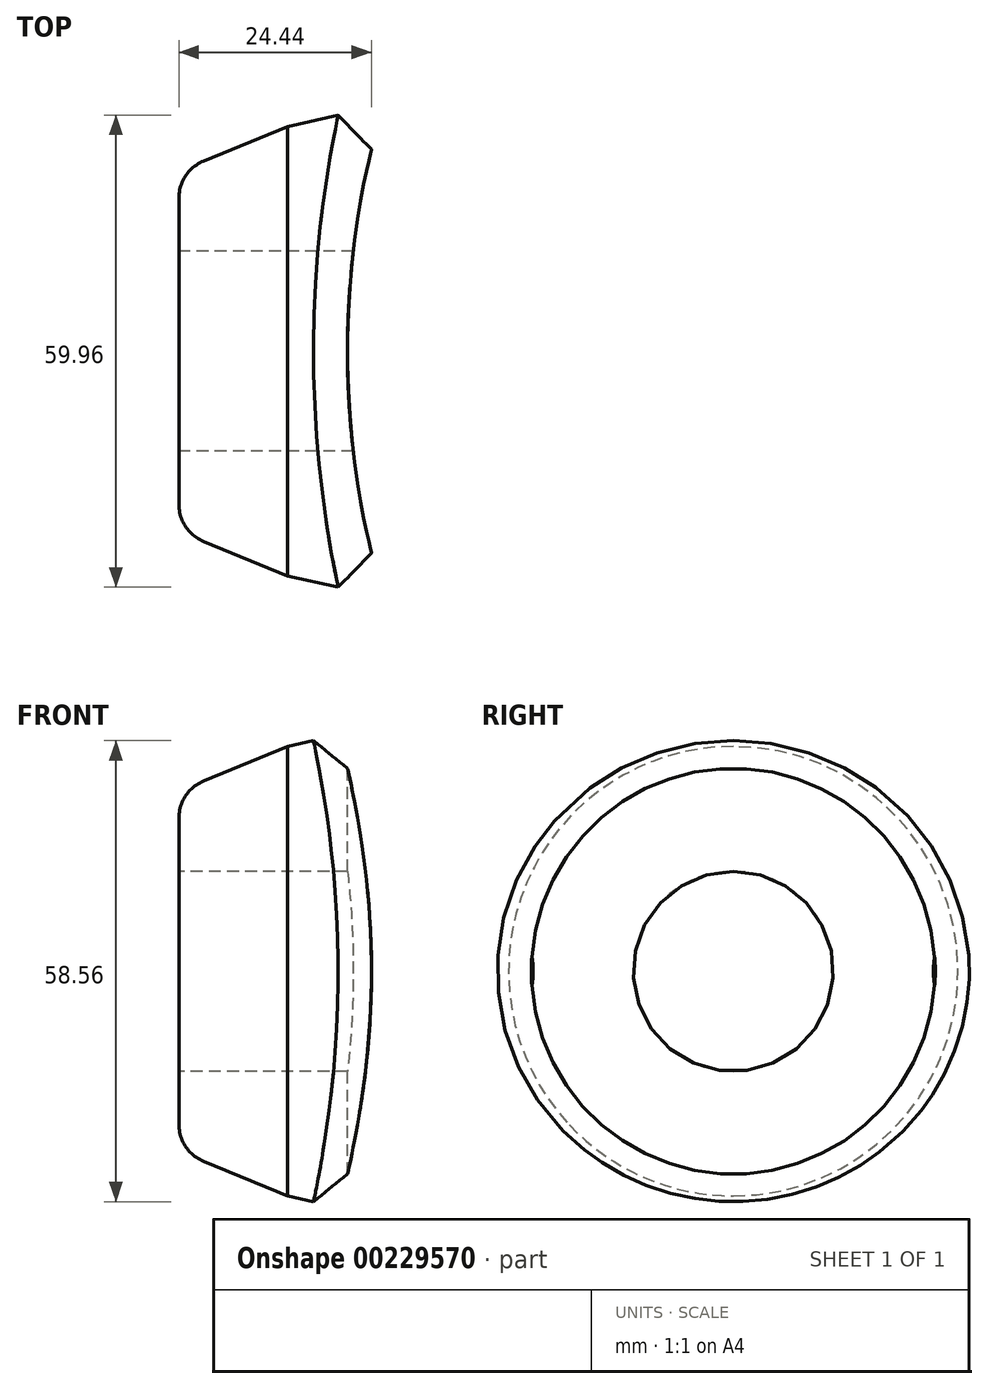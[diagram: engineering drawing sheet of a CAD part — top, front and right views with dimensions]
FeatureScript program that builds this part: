
annotation { "Feature Type Name" : "Feature", "Feature Type Description" : "" }
export const myFeature = defineFeature(function(context is Context, id is Id, definition is map)
    precondition{}
    {
        {
            var Q0;
            Q0=qCreatedBy(makeId("Front.planeOp"),FACE);
            var sketch = newSketch(context, id + "F0", { "sketchPlane" : qUnion([Q0])});
            skLineSegment(sketch, "E0", {"start": v(0, 12.7) * mm, "end": v(0, 22.86) * mm});
            skLineSegment(sketch, "E1", {"start": v(13.78, 28.54) * mm, "end": v(0, 22.86) * mm});
            skLineSegment(sketch, "E2", {"start": v(0, 12.7) * mm, "end": v(22.23, 12.7) * mm});
            skLineSegment(sketch, "E3", {"start": v(13.78, 28.54) * mm, "end": v(26.84, 31.45) * mm});
            skLineSegment(sketch, "E4", {"start": v(26.84, 31.45) * mm, "end": v(24.76, 27.52) * mm});
            skLineSegment(sketch, "E5", {"start": v(24.76, 27.52) * mm, "end": v(22.23, 12.7) * mm});
            skPoint(sketch, "E6.end.orphan", {"position": v(22.23, 22.86) * mm});
            skPoint(sketch, "E7.start.orphan", {"position": v(22.23, 0) * mm});
            skPoint(sketch, "E8.orphan", {"position": v(0, 0) * mm});
            skLineSegment(sketch, "E9", {"start": v(7.58, 0) * mm, "end": v(22.23, 0) * mm});
            skSolve(sketch);
        }
        {
            var Q0;
            Q0 = qSketchRegion(id + "F0", true);
            var Q1;
            Q1=sQuery(id+"F0.wireOp",EDGE,"E9");
            revolve(context, id + "F1", {"entities" : qUnion([Q0]), "axis" : qUnion([Q1]), "revolveType" : RevolveType.FULL});
        }
        {
            var Q0;
            Q0=qCreatedBy(makeId("Top.planeOp"),FACE);
            var sketch = newSketch(context, id + "F2", { "sketchPlane" : qUnion([Q0])});
            skLineSegment(sketch, "E10", {"start": v(21.4, 0) * mm, "end": v(130.95, 0) * mm});
            skArc(sketch, "E11", {"start": v(31.48, 45.87) * mm, "mid": v(21.4, 0) * mm, "end": v(31.48, -45.87) * mm});
            skLineSegment(sketch, "E12", {"start": v(31.48, -45.87) * mm, "end": v(31.48, 45.87) * mm});
            skSolve(sketch);
        }
        {
            var Q0;
            Q0 = qSketchRegion(id + "F2", true);
            extrude(context, id + "F3", {"entities" : qUnion([Q0]), "operationType" : NewBodyOperationType.REMOVE, "oppositeDirection" : true, "depth" : 76.2 * mm, "symmetric" : true});
        }
        {
            var Q0;
            Q0=makeQuery(id+"F3.boolean.opBoolean","INTERSECT",EDGE,{"derivedFrom":[makeQuery(id+"F1.opRevolve","SWEPT_FACE",FACE,{"disambiguationData":[OSD([sQuery(id+"F0.wireOp",EDGE,"E3")])]}),makeQuery(id+"F3.opExtrude","SWEPT_FACE",FACE,{"disambiguationData":[OSD([sQuery(id+"F2.wireOp",EDGE,"E11")])]})]});
            chamfer(context, id + "F4", {"entities" : qUnion([Q0]), "width" : 5.08 * mm, "tangentPropagation" : true});
        }
        {
            var Q0;
            Q0=makeQuery(id+"F1.opRevolve","SWEPT_EDGE",EDGE,{"disambiguationData":[OSD([sQuery(id+"F0.wireOp",EDGE,"E0"),sQuery(id+"F0.wireOp",EDGE,"E1")])]});
            fillet(context, id + "F5", {"entities" : qUnion([Q0]), "radius" : 5.08 * mm, "tangentPropagation" : true, "allowEdgeOverflow" : false});
        }
    });
